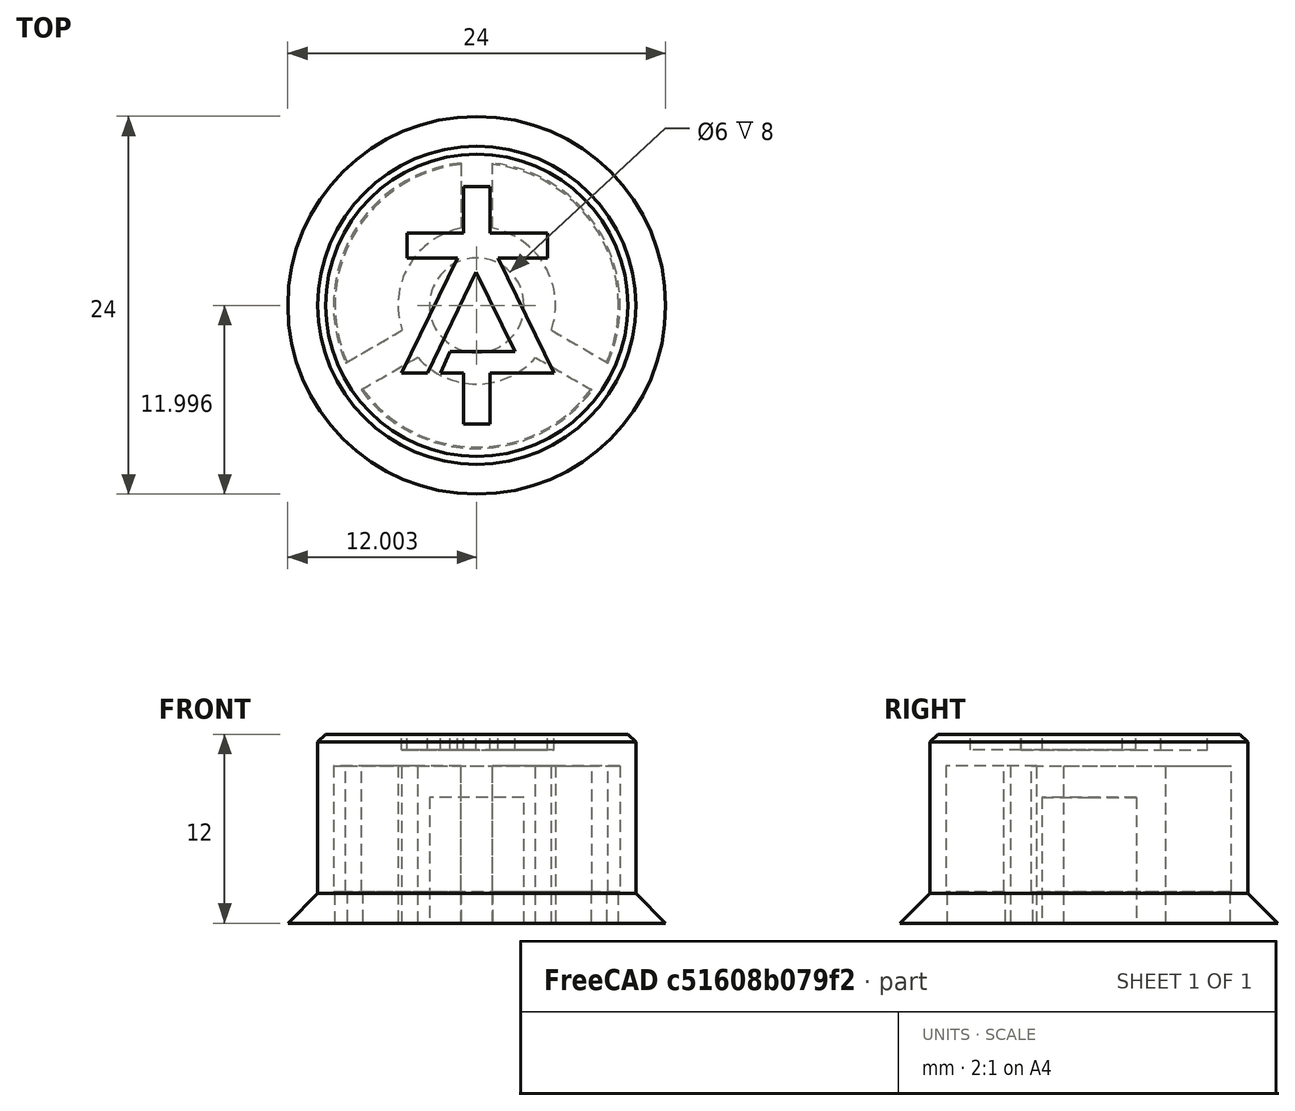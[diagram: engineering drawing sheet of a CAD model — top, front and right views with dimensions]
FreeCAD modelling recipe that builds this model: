
FCSTD DOCUMENT  (FreeCAD 0.14R3702 (Git))
Label: button2
License: CC-BY 3.0
LicenseURL: http://creativecommons.org/licenses/by/3.0/
objects: Part::Feature×18, Part::Extrusion×9, Part::Cut×6, App::DocumentObjectGroup×3, Part::RuledSurface×3, Part::MultiFuse×2, Part::Cone×1, Part::Chamfer×1
note: 40 computed .brp shape members not serialized (recipe doc carries the construction recipe); baked Part::Feature solids carry a one-line shape summary decoded from their .brp

FEATURE [App::DocumentObjectGroup] _  label="0"
FEATURE [Part::Feature] Line023 .. Line026  x4 (patterned run collapsed; names and placements below)
  shape: bbox 3.589 x 2.072 x 2e-07 mm, 0 faces, 0 solids (baked)
FEATURE [Part::Feature] Line027
  shape: bbox 2e-07 x 4.144 x 2e-07 mm, 0 faces, 0 solids (baked)
FEATURE [Part::Feature] Line028
  shape: bbox 2e-07 x 4.144 x 2e-07 mm, 0 faces, 0 solids (baked)
FEATURE [Part::Feature] Arc
  shape: bbox 14.66 x 3.711 x 2e-07 mm, 0 faces, 0 solids (baked)
FEATURE [Part::Feature] Arc001
  shape: bbox 4 x 6.482 x 2e-07 mm, 0 faces, 0 solids (baked)
FEATURE [Part::Feature] Arc002
  shape: bbox 8.098 x 12.7 x 2e-07 mm, 0 faces, 0 solids (baked)
FEATURE [Part::Feature] Arc003
  shape: bbox 8.098 x 12.7 x 2e-07 mm, 0 faces, 0 solids (baked)
FEATURE [Part::Feature] Arc004
  shape: bbox 4 x 6.482 x 2e-07 mm, 0 faces, 0 solids (baked)
FEATURE [Part::Feature] Arc005
  shape: bbox 7.485 x 1.684 x 2e-07 mm, 0 faces, 0 solids (baked)
FEATURE [App::DocumentObjectGroup] interne
  Group = -> [Line023,Line024,Line025,Line026,Line027,Line028,Arc,Arc001,Arc002,Arc003,Arc004,Arc005]
FEATURE [App::DocumentObjectGroup] button
  Group = -> [_,interne]
FEATURE [Part::Feature] Face
  Placement = pos=(0,0,11) rot=(0,0,1;0rad)
  shape: bbox 20.2 x 20.2 x 2e-07 mm, 1 faces, 0 solids (baked)
FEATURE [Part::Feature] Face001  label="logo"
  Placement = pos=(0,0,11) rot=(0,0,1;0rad)
  shape: bbox 9.684 x 15.06 x 2e-07 mm, 1 faces, 0 solids (baked)
FEATURE [Part::Extrusion] Extrude
  Base = -> Face001
  Dir = (0,0,1)
  Solid = false
FEATURE [Part::Extrusion] Extrude002
  Base = -> Face
  Dir = (0,0,1)
  Solid = false
FEATURE [Part::Cut] Cut
  Base = -> Extrude002
  Tool = -> Extrude
FEATURE [Part::Feature] Face002  label="logo001"
  Placement = pos=(0,0,11) rot=(0,0,1;0rad)
  shape: bbox 9.684 x 15.06 x 2e-07 mm, 1 faces, 0 solids (baked)
FEATURE [Part::Extrusion] Extrude003  label="Ext_logo"
  Base = -> Face002
  Dir = (0,0,1)
  Solid = false
FEATURE [Part::Feature] Face003
  shape: bbox 20.2 x 20.2 x 2e-07 mm, 1 faces, 0 solids (baked)
FEATURE [Part::RuledSurface] Ruled_Surface
  Curve1 = -> Arc003 [Edge1]
  Curve2 = -> Arc004 [Edge1]
  Orientation = 0
FEATURE [Part::RuledSurface] Ruled_Surface001
  Curve1 = -> Arc001 [Edge1]
  Curve2 = -> Arc002 [Edge1]
  Orientation = 0
FEATURE [Part::RuledSurface] Ruled_Surface002
  Curve1 = -> Arc005 [Edge1]
  Curve2 = -> Arc [Edge1]
  Orientation = 0
FEATURE [Part::Feature] Face004
  shape: bbox 6 x 6 x 2e-07 mm, 1 faces, 0 solids (baked)
FEATURE [Part::Extrusion] Extrude006
  Base = -> Ruled_Surface
  Dir = (0,0,10)
  Solid = false
FEATURE [Part::Extrusion] Extrude007
  Base = -> Ruled_Surface001
  Dir = (0,0,10)
  Solid = false
FEATURE [Part::Extrusion] Extrude008
  Base = -> Ruled_Surface002
  Dir = (0,0,10)
  Solid = false
FEATURE [Part::Extrusion] Extrude009
  Base = -> Face004
  Dir = (0,0,8)
  Solid = false
FEATURE [Part::Feature] Face005
  Placement = pos=(0,0,10) rot=(0,0,1;0rad)
  shape: bbox 20.2 x 20.2 x 2e-07 mm, 1 faces, 0 solids (baked)
FEATURE [Part::Extrusion] Extrude011
  Base = -> Face005
  Dir = (0,0,1)
  Solid = false
FEATURE [Part::MultiFuse] Fusion  label="dessus"
  Shapes = -> [Extrude011,Cut]
FEATURE [Part::Extrusion] Extrude012
  Base = -> Face003
  Dir = (0,0,10)
  Solid = false
FEATURE [Part::Cut] Cut001
  Base = -> Extrude012
  Tool = -> Extrude007
FEATURE [Part::Cut] Cut002
  Base = -> Cut001
  Tool = -> Extrude008
FEATURE [Part::Cut] Cut003
  Base = -> Cut002
  Tool = -> Extrude006
FEATURE [Part::Cut] Cut004  label="corps"
  Base = -> Cut003
  Tool = -> Extrude009
FEATURE [Part::Cone] Cone  label="Cône"
  Angle = 360
  Height = 2
  Placement = pos=(0,1.50556,0) rot=(0,0,1;0rad)
  Radius1 = 12
  Radius2 = 10
FEATURE [Part::Cut] Cut005  label="bague"
  Base = -> Cone
FEATURE [Part::MultiFuse] Fusion001  label="boutonH"
  Shapes = -> [Fusion,Cut005,Cut004]
FEATURE [Part::Chamfer] Chamfer  label="B_final"
  Base = -> Fusion001
  Edges = 1 edges r=0.5: [Edge3]
